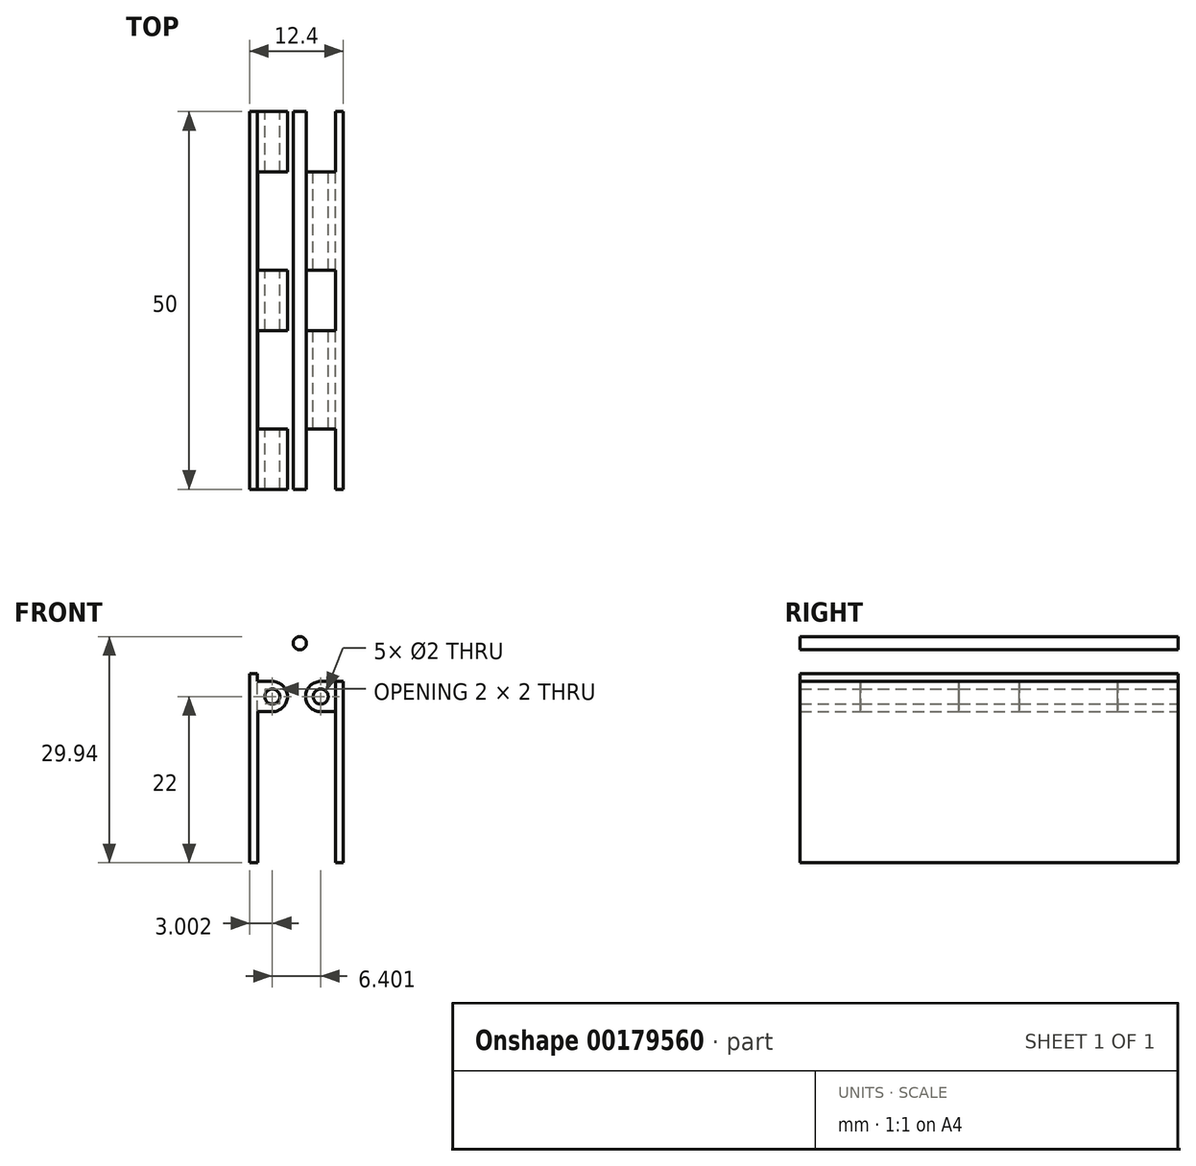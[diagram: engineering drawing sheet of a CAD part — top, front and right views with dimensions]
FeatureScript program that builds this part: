
annotation { "Feature Type Name" : "Feature", "Feature Type Description" : "" }
export const myFeature = defineFeature(function(context is Context, id is Id, definition is map)
    precondition{}
    {
        {
            var Q0;
            Q0=qCreatedBy(makeId("Front.planeOp"),FACE);
            var sketch = newSketch(context, id + "F0", { "sketchPlane" : qUnion([Q0])});
            skLineSegment(sketch, "E0.top", {"start": v(11.51, -18.22) * mm, "end": v(12.51, -18.22) * mm});
            skLineSegment(sketch, "E0.left", {"start": v(11.51, 5.77) * mm, "end": v(11.51, -18.22) * mm});
            skLineSegment(sketch, "E0.right", {"start": v(12.51, 5.78) * mm, "end": v(12.51, -18.22) * mm});
            skLineSegment(sketch, "E1.bottom", {"start": v(11.51, 5.78) * mm, "end": v(9.51, 5.78) * mm});
            skLineSegment(sketch, "E1.top", {"start": v(11.51, 1.78) * mm, "end": v(9.51, 1.78) * mm});
            skLineSegment(sketch, "E1.left", {"start": v(11.51, 5.78) * mm, "end": v(11.51, 1.78) * mm});
            skLineSegment(sketch, "E1.right", {"start": v(7.51, 3.78) * mm, "end": v(7.51, 3.78) * mm});
            skLineSegment(sketch, "E2", {"start": v(11.51, 5.78) * mm, "end": v(7.51, 1.78) * mm, "construction": true});
            skLineSegment(sketch, "E3", {"start": v(7.51, 5.78) * mm, "end": v(11.51, 1.78) * mm, "construction": true});
            skCircle(sketch, "E4", {"center": v(9.51, 3.78) * mm, "radius": 1 * mm});
            skPoint(sketch, "E5.visualSharp", {"position": v(7.51, 5.78) * mm});
            skArc(sketch, "E5.filletArc", {"start": v(9.51, 5.78) * mm, "mid": v(8.1, 5.2) * mm, "end": v(7.51, 3.78) * mm});
            skPoint(sketch, "E6.visualSharp", {"position": v(7.51, 1.78) * mm});
            skArc(sketch, "E6.filletArc", {"start": v(7.51, 3.78) * mm, "mid": v(8.1, 2.37) * mm, "end": v(9.51, 1.78) * mm});
            skLineSegment(sketch, "E7.MirrorCS", {"start": v(18.7, 6.78) * mm, "end": v(17.7, 6.78) * mm});
            skLineSegment(sketch, "E8.MirrorCS", {"start": v(18.76, -18.22) * mm, "end": v(17.7, -18.22) * mm});
            skArc(sketch, "E9.MirrorCS", {"start": v(22.7, 3.78) * mm, "mid": v(22.11, 2.37) * mm, "end": v(20.7, 1.78) * mm});
            skLineSegment(sketch, "E10.MirrorCS", {"start": v(18.7, 5.78) * mm, "end": v(22.7, 1.78) * mm, "construction": true});
            skPoint(sketch, "E11.MirrorP", {"position": v(22.7, 5.78) * mm});
            skLineSegment(sketch, "E12.MirrorCS", {"start": v(22.7, 5.78) * mm, "end": v(18.7, 1.78) * mm, "construction": true});
            skPoint(sketch, "E13.MirrorP", {"position": v(22.7, 1.78) * mm});
            skLineSegment(sketch, "E14.MirrorCS", {"start": v(22.7, 3.78) * mm, "end": v(22.7, 3.78) * mm});
            skLineSegment(sketch, "E15.MirrorCS", {"start": v(18.7, 1.78) * mm, "end": v(20.7, 1.78) * mm});
            skArc(sketch, "E16.MirrorCS", {"start": v(20.7, 5.78) * mm, "mid": v(22.11, 5.2) * mm, "end": v(22.7, 3.78) * mm});
            skCircle(sketch, "E17.MirrorC", {"center": v(20.7, 3.78) * mm, "radius": 1 * mm});
            skLineSegment(sketch, "E18.MirrorCS", {"start": v(17.7, 6.78) * mm, "end": v(17.7, -18.22) * mm});
            skLineSegment(sketch, "E19", {"start": v(11.51, 5.78) * mm, "end": v(12.51, 5.78) * mm});
            skLineSegment(sketch, "E20", {"start": v(18.76, 1.78) * mm, "end": v(18.76, -18.22) * mm});
            skPoint(sketch, "E21.orphan", {"position": v(19.82, -18.22) * mm});
            skLineSegment(sketch, "E22", {"start": v(19.7, 5.78) * mm, "end": v(20.7, 5.78) * mm});
            skLineSegment(sketch, "E23", {"start": v(19.7, 5.78) * mm, "end": v(18.7, 5.78) * mm});
            skLineSegment(sketch, "E24", {"start": v(18.7, 5.78) * mm, "end": v(18.7, 6.78) * mm});
            skPoint(sketch, "E25.orphan", {"position": v(19.7, 6.78) * mm});
            skSolve(sketch);
        }
        {
            var Q0;
            Q0=qSketchRegion(id+"F0",true);
            extrude(context, id + "F1", {"entities" : qUnion([Q0]), "depth" : 50 * mm});
        }
        {
            var Q0;
            Q0=makeQuery(id+"F1.opExtrude","SWEPT_BODY",BODY,{"disambiguationData":[OSD([sQuery(id+"F0.wireOp",EDGE,"E7.MirrorCS"),sQuery(id+"F0.wireOp",EDGE,"E8.MirrorCS"),sQuery(id+"F0.wireOp",EDGE,"E9.MirrorCS"),sQuery(id+"F0.wireOp",EDGE,"E15.MirrorCS"),sQuery(id+"F0.wireOp",EDGE,"E16.MirrorCS"),sQuery(id+"F0.wireOp",EDGE,"E72.MirrorCS"),sQuery(id+"F0.wireOp",EDGE,"E17.MirrorC"),sQuery(id+"F0.wireOp",EDGE,"E74.MirrorCS"),sQuery(id+"F0.wireOp",EDGE,"E18.MirrorCS")])]});
            transform(context, id + "F2", {"entities" : qUnion([Q0]), "transformType" : TransformType.TRANSLATION_3D, "dx" : -17.58 * mm, "dy" : 0 * mm, "dz" : 0 * mm, "makeCopy" : false});
        }
        {
            var Q0;
            Q0=makeQuery(id+"F1.opExtrude","SWEPT_FACE",FACE,{"disambiguationData":[OSD([sQuery(id+"F0.wireOp",EDGE,"E7.MirrorCS")])]});
            var sketch = newSketch(context, id + "F3", { "sketchPlane" : qUnion([Q0])});
            skLineSegment(sketch, "E26", {"start": v(6.47, 0) * mm, "end": v(6.47, -8) * mm, "construction": true});
            skLineSegment(sketch, "E27", {"start": v(6.47, -8) * mm, "end": v(6.47, -21) * mm, "construction": true});
            skLineSegment(sketch, "E28", {"start": v(6.47, -21) * mm, "end": v(6.47, -29) * mm, "construction": true});
            skLineSegment(sketch, "E29", {"start": v(6.47, -29) * mm, "end": v(6.47, -42) * mm, "construction": true});
            skLineSegment(sketch, "E30", {"start": v(6.47, -42) * mm, "end": v(6.47, -50) * mm, "construction": true});
            skLineSegment(sketch, "E31", {"start": v(11.59, 0) * mm, "end": v(11.59, -50.12) * mm, "construction": true});
            skLineSegment(sketch, "E32", {"start": v(11.59, -50.12) * mm, "end": v(1.11, -50) * mm, "construction": true});
            skLineSegment(sketch, "E33", {"start": v(1.11, -50) * mm, "end": v(1.11, 0) * mm, "construction": true});
            skLineSegment(sketch, "E34.bottom", {"start": v(6.47, -8) * mm, "end": v(11.59, -8) * mm});
            skLineSegment(sketch, "E34.top", {"start": v(6.47, 0) * mm, "end": v(11.59, 0) * mm});
            skLineSegment(sketch, "E34.left", {"start": v(6.47, -8) * mm, "end": v(6.47, 0) * mm});
            skLineSegment(sketch, "E34.right", {"start": v(11.59, -8) * mm, "end": v(11.59, 0) * mm});
            skLineSegment(sketch, "E35.bottom", {"start": v(6.47, -8) * mm, "end": v(1.11, -8) * mm});
            skLineSegment(sketch, "E35.top", {"start": v(6.47, -20.99) * mm, "end": v(1.11, -20.99) * mm});
            skLineSegment(sketch, "E35.left", {"start": v(6.47, -8) * mm, "end": v(6.47, -20.99) * mm});
            skLineSegment(sketch, "E35.right", {"start": v(1.11, -8) * mm, "end": v(1.11, -20.99) * mm});
            skLineSegment(sketch, "E36.bottom", {"start": v(6.47, -20.99) * mm, "end": v(11.59, -20.99) * mm});
            skLineSegment(sketch, "E36.top", {"start": v(6.47, -29.03) * mm, "end": v(11.59, -29.03) * mm});
            skLineSegment(sketch, "E36.left", {"start": v(6.47, -20.99) * mm, "end": v(6.47, -29.03) * mm});
            skLineSegment(sketch, "E36.right", {"start": v(11.59, -20.99) * mm, "end": v(11.59, -29.03) * mm});
            skLineSegment(sketch, "E37.bottom", {"start": v(6.47, -29) * mm, "end": v(1.11, -29) * mm});
            skLineSegment(sketch, "E37.top", {"start": v(6.47, -42.01) * mm, "end": v(1.11, -42.01) * mm});
            skLineSegment(sketch, "E37.left", {"start": v(6.47, -29) * mm, "end": v(6.47, -42.01) * mm});
            skLineSegment(sketch, "E37.right", {"start": v(1.11, -29) * mm, "end": v(1.11, -42.01) * mm});
            skLineSegment(sketch, "E38.bottom", {"start": v(6.47, -42.01) * mm, "end": v(11.59, -42.01) * mm});
            skLineSegment(sketch, "E38.top", {"start": v(6.47, -50.12) * mm, "end": v(11.59, -50.12) * mm});
            skLineSegment(sketch, "E38.left", {"start": v(6.47, -42.01) * mm, "end": v(6.47, -50.12) * mm});
            skLineSegment(sketch, "E38.right", {"start": v(11.59, -42.01) * mm, "end": v(11.59, -50.12) * mm});
            skSolve(sketch);
        }
        {
            var Q0;
            Q0=qSketchRegion(id+"F3",true);
            extrude(context, id + "F4", {"entities" : qUnion([Q0]), "operationType" : NewBodyOperationType.REMOVE, "oppositeDirection" : true, "depth" : 5 * mm});
        }
        {
            var Q0;
            Q0=qCreatedBy(makeId("Front.planeOp"),FACE);
            var sketch = newSketch(context, id + "F5", { "sketchPlane" : qUnion([Q0])});
            skCircle(sketch, "E39", {"center": v(6.76, 10.84) * mm, "radius": 0.88 * mm});
            skSolve(sketch);
        }
        {
            var Q0;
            Q0=qSketchRegion(id+"F5",true);
            extrude(context, id + "F6", {"entities" : qUnion([Q0]), "depth" : 50 * mm});
        }
        {
            var Q0;
            Q0=makeQuery(id+"F1.opExtrude","CAP_FACE",FACE,{"disambiguationData":[OSD([sQuery(id+"F0.wireOp",EDGE,"E0.top"),sQuery(id+"F0.wireOp",EDGE,"E0.left"),sQuery(id+"F0.wireOp",EDGE,"E0.right"),sQuery(id+"F0.wireOp",EDGE,"E1.bottom"),sQuery(id+"F0.wireOp",EDGE,"E1.top"),sQuery(id+"F0.wireOp",EDGE,"E4"),sQuery(id+"F0.wireOp",EDGE,"E5.filletArc"),sQuery(id+"F0.wireOp",EDGE,"E6.filletArc"),sQuery(id+"F0.wireOp",EDGE,"E19")])],"isStart":false});
            var sketch = newSketch(context, id + "F7", { "sketchPlane" : qUnion([Q0])});
            skLineSegment(sketch, "E40.bottom", {"start": v(11.51, 1.78) * mm, "end": v(12.51, 1.78) * mm});
            skLineSegment(sketch, "E40.top", {"start": v(11.51, 5.78) * mm, "end": v(12.51, 5.78) * mm});
            skLineSegment(sketch, "E40.left", {"start": v(11.51, 1.78) * mm, "end": v(11.51, 5.78) * mm});
            skLineSegment(sketch, "E40.right", {"start": v(12.51, 1.78) * mm, "end": v(12.51, 5.78) * mm});
            skSolve(sketch);
        }
        {
            var Q0;
            Q0=qSketchRegion(id+"F7",true);
            extrude(context, id + "F8", {"entities" : qUnion([Q0]), "operationType" : NewBodyOperationType.ADD, "oppositeDirection" : true, "depth" : 50 * mm});
        }
    });
